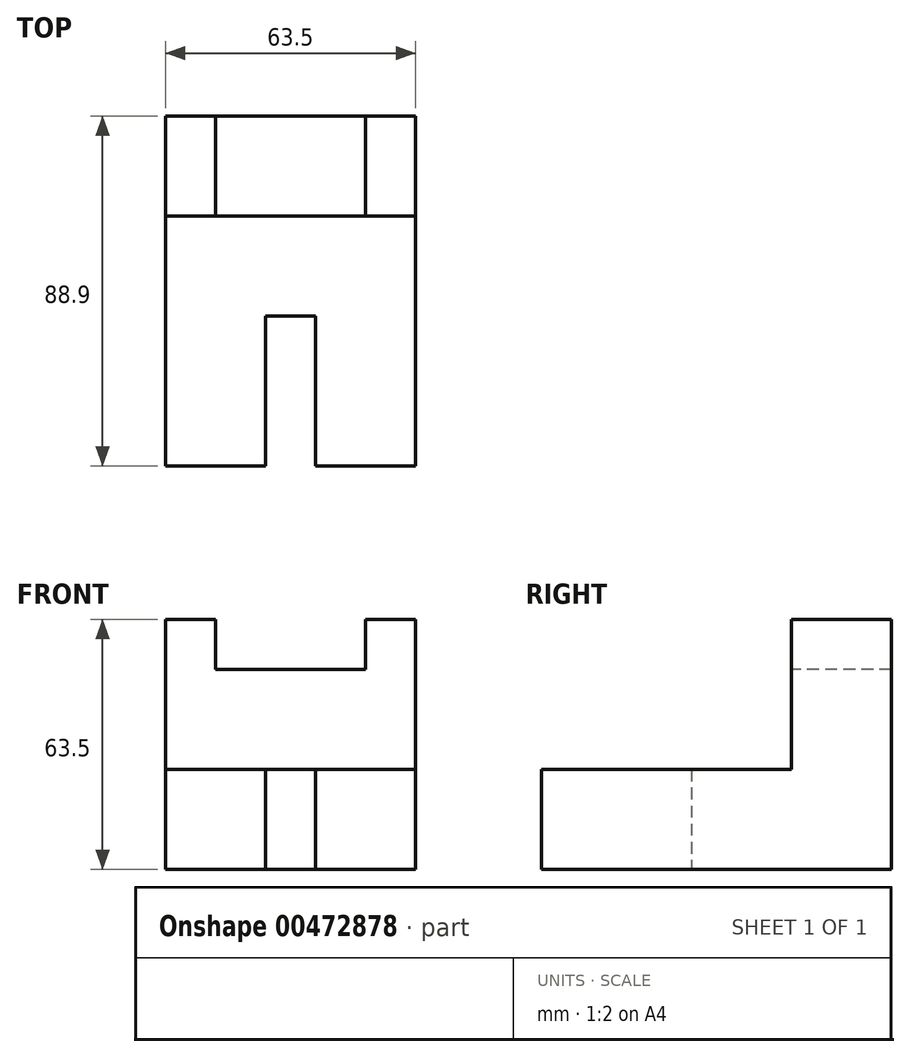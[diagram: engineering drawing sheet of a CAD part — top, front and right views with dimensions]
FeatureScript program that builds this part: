
annotation { "Feature Type Name" : "Feature", "Feature Type Description" : "" }
export const myFeature = defineFeature(function(context is Context, id is Id, definition is map)
    precondition{}
    {
        {
            var Q0;
            Q0=qCreatedBy(makeId("Right.planeOp"),FACE);
            var sketch = newSketch(context, id + "F0", { "sketchPlane" : qUnion([Q0])});
            skLineSegment(sketch, "E0", {"start": v(-56.32, 10.73) * mm, "end": v(-56.32, -14.67) * mm});
            skLineSegment(sketch, "E1", {"start": v(-56.32, -14.67) * mm, "end": v(32.58, -14.67) * mm});
            skLineSegment(sketch, "E2", {"start": v(32.58, -14.67) * mm, "end": v(32.58, 48.83) * mm});
            skLineSegment(sketch, "E3", {"start": v(32.58, 48.83) * mm, "end": v(7.18, 48.83) * mm});
            skLineSegment(sketch, "E4", {"start": v(7.18, 48.83) * mm, "end": v(7.18, 10.73) * mm});
            skLineSegment(sketch, "E5", {"start": v(7.18, 10.73) * mm, "end": v(-56.32, 10.73) * mm});
            skSolve(sketch);
        }
        {
            var Q0;
            Q0 = qSketchRegion(id + "F0", true);
            extrude(context, id + "F1", {"entities" : qUnion([Q0]), "depth" : 63.5 * mm});
        }
        {
            var Q0;
            Q0=makeQuery(id+"F1.opExtrude","SWEPT_FACE",FACE,{"disambiguationData":[OSD([sQuery(id+"F0.wireOp",EDGE,"E0")])]});
            var sketch = newSketch(context, id + "F2", { "sketchPlane" : qUnion([Q0])});
            skLineSegment(sketch, "E6", {"start": v(25.4, 10.73) * mm, "end": v(25.4, -14.67) * mm});
            skLineSegment(sketch, "E7", {"start": v(25.4, -14.67) * mm, "end": v(38.1, -14.67) * mm});
            skLineSegment(sketch, "E8", {"start": v(38.1, -14.67) * mm, "end": v(38.1, 10.73) * mm});
            skLineSegment(sketch, "E9", {"start": v(38.1, 10.73) * mm, "end": v(25.4, 10.73) * mm});
            skSolve(sketch);
        }
        {
            var Q0;
            Q0 = qSketchRegion(id + "F2", true);
            extrude(context, id + "F3", {"entities" : qUnion([Q0]), "operationType" : NewBodyOperationType.REMOVE, "oppositeDirection" : true, "depth" : 38.1 * mm});
        }
        {
            var Q0;
            Q0=makeQuery(id+"F1.opExtrude","SWEPT_FACE",FACE,{"disambiguationData":[OSD([sQuery(id+"F0.wireOp",EDGE,"E3")])]});
            var sketch = newSketch(context, id + "F4", { "sketchPlane" : qUnion([Q0])});
            skLineSegment(sketch, "E10", {"start": v(12.7, 32.58) * mm, "end": v(12.7, 7.18) * mm});
            skLineSegment(sketch, "E11", {"start": v(12.7, 7.18) * mm, "end": v(50.8, 7.18) * mm});
            skLineSegment(sketch, "E12", {"start": v(50.8, 7.18) * mm, "end": v(50.8, 32.58) * mm});
            skLineSegment(sketch, "E13", {"start": v(50.8, 32.58) * mm, "end": v(12.7, 32.58) * mm});
            skSolve(sketch);
        }
        {
            var Q0;
            Q0 = qSketchRegion(id + "F4", true);
            extrude(context, id + "F5", {"entities" : qUnion([Q0]), "operationType" : NewBodyOperationType.REMOVE, "oppositeDirection" : true, "depth" : 12.7 * mm});
        }
    });
